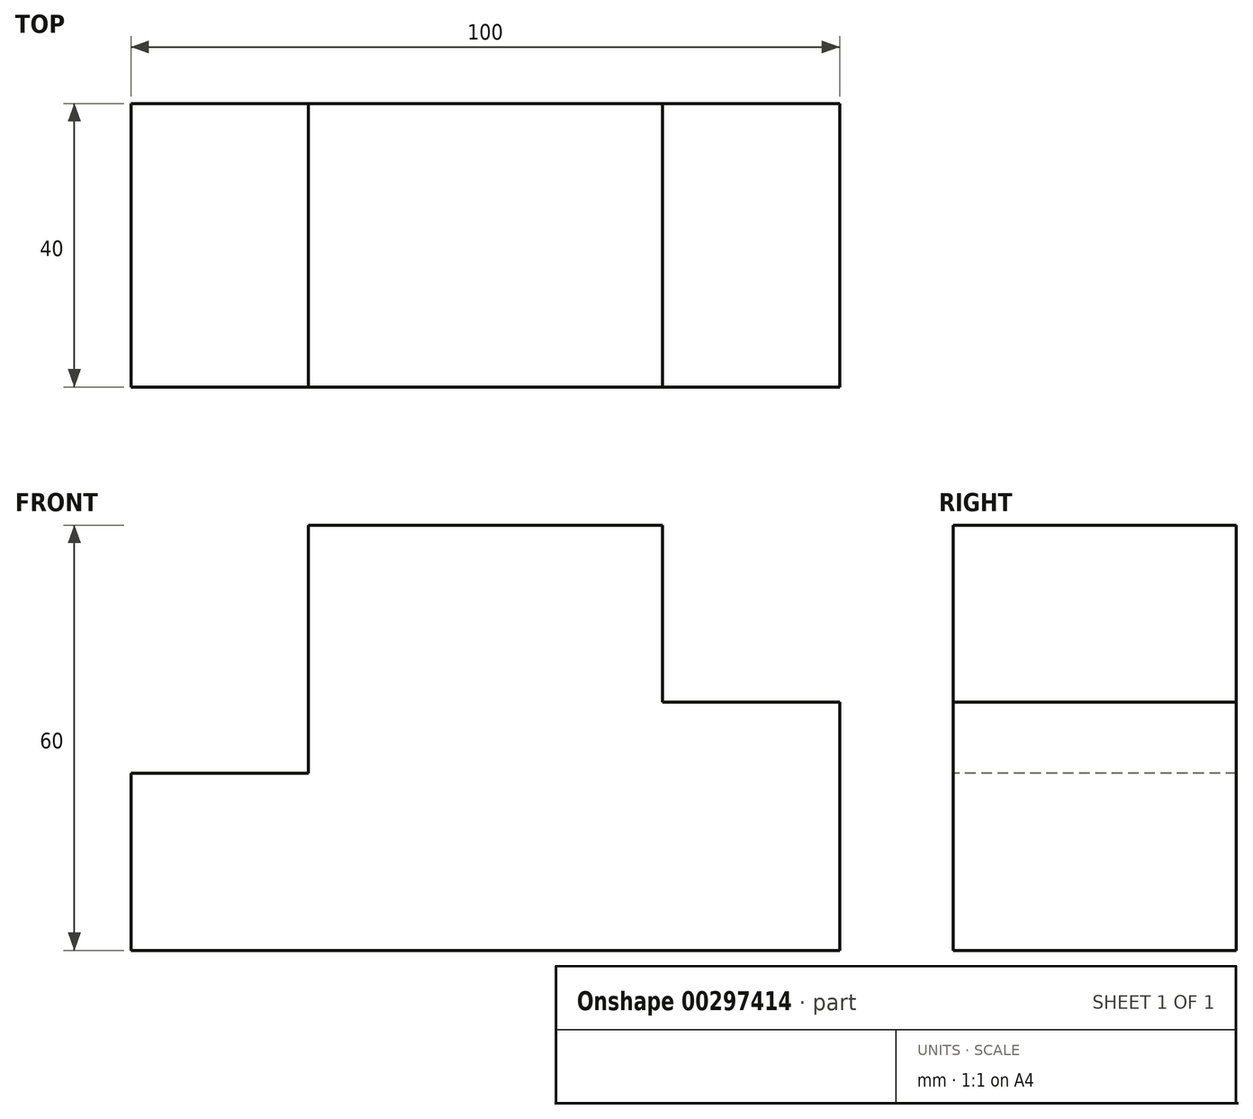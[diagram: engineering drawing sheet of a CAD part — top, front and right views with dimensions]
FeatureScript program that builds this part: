
annotation { "Feature Type Name" : "Feature", "Feature Type Description" : "" }
export const myFeature = defineFeature(function(context is Context, id is Id, definition is map)
    precondition{}
    {
        {
            var Q0;
            Q0=qCreatedBy(makeId("Front.planeOp"),FACE);
            var sketch = newSketch(context, id + "F0", { "sketchPlane" : qUnion([Q0])});
            skLineSegment(sketch, "E0.bottom", {"start": v(50, 30) * mm, "end": v(-50, 30) * mm});
            skLineSegment(sketch, "E0.top", {"start": v(50, -30) * mm, "end": v(-50, -30) * mm});
            skLineSegment(sketch, "E0.left", {"start": v(50, 30) * mm, "end": v(50, -30) * mm});
            skLineSegment(sketch, "E0.right", {"start": v(-50, 30) * mm, "end": v(-50, -30) * mm});
            skPoint(sketch, "E0.middle", {"position": v(0, 0) * mm});
            skSolve(sketch);
        }
        {
            var Q0;
            Q0 = qSketchRegion(id + "F0", true);
            extrude(context, id + "F1", {"entities" : qUnion([Q0]), "depth" : 40 * mm});
        }
        {
            var Q0;
            Q0=makeQuery(id+"F1.opExtrude","CAP_FACE",FACE,{"disambiguationData":[OSD([sQuery(id+"F0.wireOp",EDGE,"E0.bottom"),sQuery(id+"F0.wireOp",EDGE,"E0.top"),sQuery(id+"F0.wireOp",EDGE,"E0.left"),sQuery(id+"F0.wireOp",EDGE,"E0.right")])],"isStart":false});
            var sketch = newSketch(context, id + "F2", { "sketchPlane" : qUnion([Q0])});
            skLineSegment(sketch, "E1.bottom", {"start": v(-50, -5) * mm, "end": v(-25, -5) * mm});
            skLineSegment(sketch, "E1.top", {"start": v(-50, 30) * mm, "end": v(-25, 30) * mm});
            skLineSegment(sketch, "E1.left", {"start": v(-50, -5) * mm, "end": v(-50, 30) * mm});
            skLineSegment(sketch, "E1.right", {"start": v(-25, -5) * mm, "end": v(-25, 30) * mm});
            skLineSegment(sketch, "E2.bottom", {"start": v(50, 5) * mm, "end": v(25, 5) * mm});
            skLineSegment(sketch, "E2.top", {"start": v(50, 30) * mm, "end": v(25, 30) * mm});
            skLineSegment(sketch, "E2.left", {"start": v(50, 5) * mm, "end": v(50, 30) * mm});
            skLineSegment(sketch, "E2.right", {"start": v(25, 5) * mm, "end": v(25, 30) * mm});
            skSolve(sketch);
        }
        {
            var Q0;
            Q0 = qSketchRegion(id + "F2", true);
            extrude(context, id + "F3", {"entities" : qUnion([Q0]), "operationType" : NewBodyOperationType.REMOVE, "endBound" : BoundingType.THROUGH_ALL, "oppositeDirection" : true, "depth" : 25.4 * mm});
        }
    });
